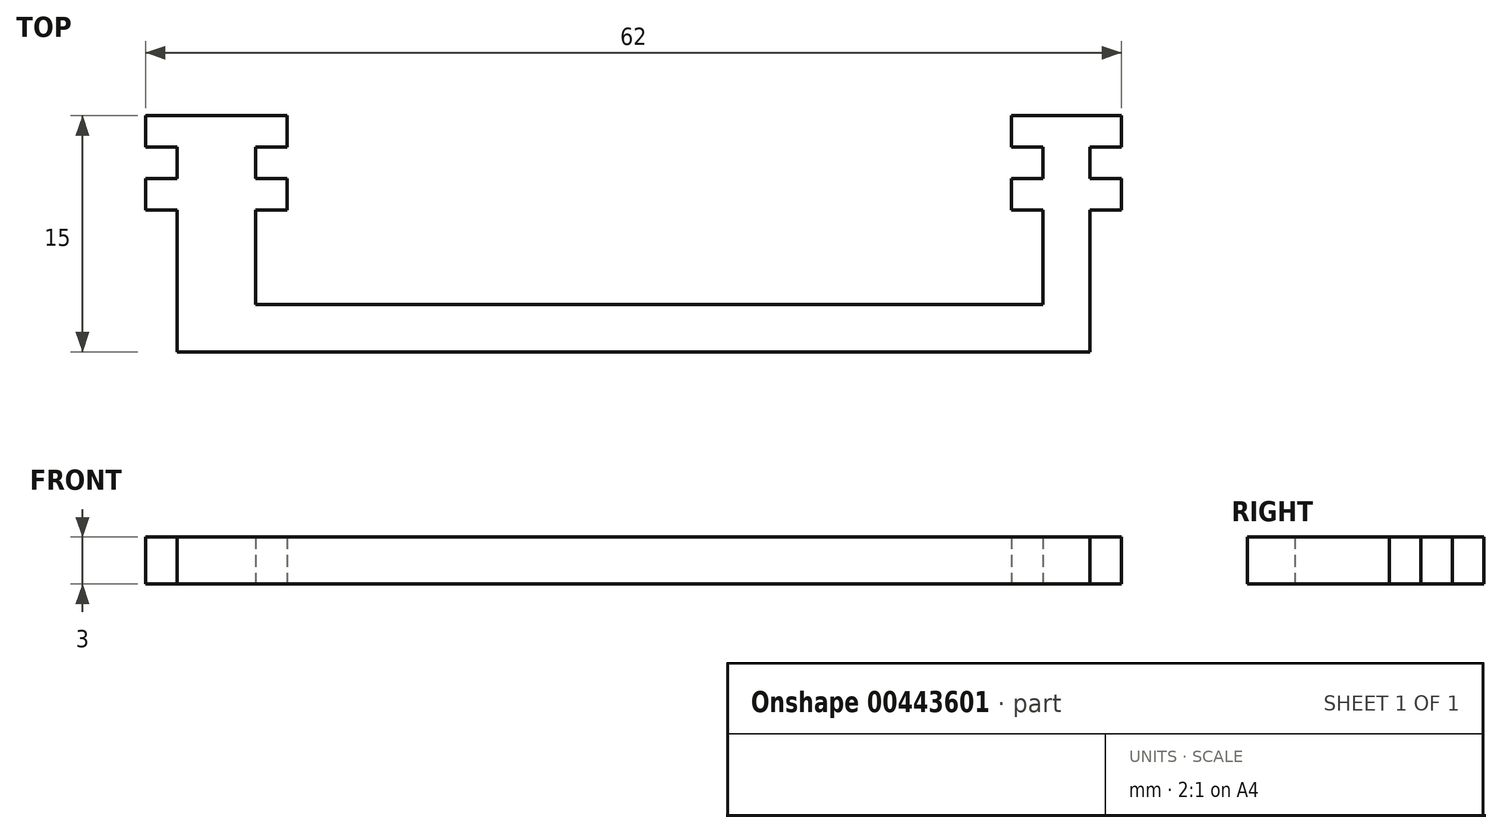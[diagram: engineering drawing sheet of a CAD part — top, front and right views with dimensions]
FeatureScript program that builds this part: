
annotation { "Feature Type Name" : "Feature", "Feature Type Description" : "" }
export const myFeature = defineFeature(function(context is Context, id is Id, definition is map)
    precondition{}
    {
        {
            var Q0;
            Q0=qCreatedBy(makeId("Top.planeOp"),FACE);
            var sketch = newSketch(context, id + "F0", { "sketchPlane" : qUnion([Q0])});
            skLineSegment(sketch, "E0.bottom", {"start": v(-3.5, 0) * mm, "end": v(3.5, 0) * mm});
            skLineSegment(sketch, "E0.left", {"start": v(-3.5, 0) * mm, "end": v(-3.5, -2) * mm});
            skLineSegment(sketch, "E0.right", {"start": v(3.5, 0) * mm, "end": v(3.5, -2) * mm});
            skLineSegment(sketch, "E1.left", {"start": v(-1.5, -6) * mm, "end": v(-1.5, -12) * mm});
            skLineSegment(sketch, "E1.right", {"start": v(1.5, -6) * mm, "end": v(1.5, -15) * mm});
            skLineSegment(sketch, "E2", {"start": v(-3.5, -2) * mm, "end": v(-1.5, -2) * mm});
            skLineSegment(sketch, "E3", {"start": v(3.5, -4) * mm, "end": v(1.5, -4) * mm});
            skLineSegment(sketch, "E4", {"start": v(-1.5, -2) * mm, "end": v(-1.5, -4) * mm});
            skLineSegment(sketch, "E5", {"start": v(1.5, -4) * mm, "end": v(1.5, -2) * mm});
            skLineSegment(sketch, "E6.trimOffspring", {"start": v(1.5, -2) * mm, "end": v(3.5, -2) * mm});
            skLineSegment(sketch, "E7.trimOffspring", {"start": v(-1.5, -4) * mm, "end": v(-3.5, -4) * mm});
            skLineSegment(sketch, "E8.trimOffspring", {"start": v(3.5, -4) * mm, "end": v(3.5, -6) * mm});
            skLineSegment(sketch, "E9.trimOffspring", {"start": v(-3.5, -4) * mm, "end": v(-3.5, -6) * mm});
            skLineSegment(sketch, "E10", {"start": v(-3.5, -6) * mm, "end": v(-1.5, -6) * mm});
            skLineSegment(sketch, "E11", {"start": v(1.5, -6) * mm, "end": v(3.5, -6) * mm});
            skLineSegment(sketch, "E12", {"start": v(1.5, -15) * mm, "end": v(-56.5, -15) * mm});
            skLineSegment(sketch, "E13.bottom", {"start": v(-49.5, 0) * mm, "end": v(-58.5, 0) * mm});
            skLineSegment(sketch, "E13.top", {"start": v(-49.5, -2) * mm, "end": v(-51.5, -2) * mm});
            skLineSegment(sketch, "E13.left", {"start": v(-49.5, 0) * mm, "end": v(-49.5, -2) * mm});
            skLineSegment(sketch, "E13.right", {"start": v(-58.5, 0) * mm, "end": v(-58.5, -2) * mm});
            skLineSegment(sketch, "E14.bottom", {"start": v(-49.5, -4) * mm, "end": v(-51.5, -4) * mm});
            skLineSegment(sketch, "E14.top", {"start": v(-49.5, -6) * mm, "end": v(-51.5, -6) * mm});
            skLineSegment(sketch, "E14.left", {"start": v(-49.5, -4) * mm, "end": v(-49.5, -6) * mm});
            skLineSegment(sketch, "E14.right", {"start": v(-58.5, -4) * mm, "end": v(-58.5, -6) * mm});
            skLineSegment(sketch, "E15.left", {"start": v(-56.5, -2) * mm, "end": v(-56.5, -4) * mm});
            skLineSegment(sketch, "E15.right", {"start": v(-51.5, -2) * mm, "end": v(-51.5, -4) * mm});
            skLineSegment(sketch, "E16.trimOffspring", {"start": v(-56.5, -6) * mm, "end": v(-58.5, -6) * mm});
            skLineSegment(sketch, "E17.trimOffspring", {"start": v(-56.5, -6) * mm, "end": v(-56.5, -15) * mm});
            skLineSegment(sketch, "E18.trimOffspring", {"start": v(-56.5, -4) * mm, "end": v(-58.5, -4) * mm});
            skLineSegment(sketch, "E19.trimOffspring", {"start": v(-51.5, -6) * mm, "end": v(-51.5, -12) * mm});
            skLineSegment(sketch, "E20.trimOffspring", {"start": v(-56.5, -2) * mm, "end": v(-58.5, -2) * mm});
            skLineSegment(sketch, "E21", {"start": v(-51.5, -12) * mm, "end": v(-1.5, -12) * mm});
            skSolve(sketch);
        }
        {
            var Q0;
            Q0=makeQuery(id+"F0.imprint","IMPRINT",FACE,{"disambiguationData":[TD([[makeQuery(id+"F0.imprint","IMPRINT",EDGE,{"derivedFrom":sQuery(id+"F0.wireOp",EDGE,"E0.bottom")}),-1.0]])]});
            extrude(context, id + "F1", {"entities" : qUnion([Q0]), "depth" : 3 * mm});
        }
    });
